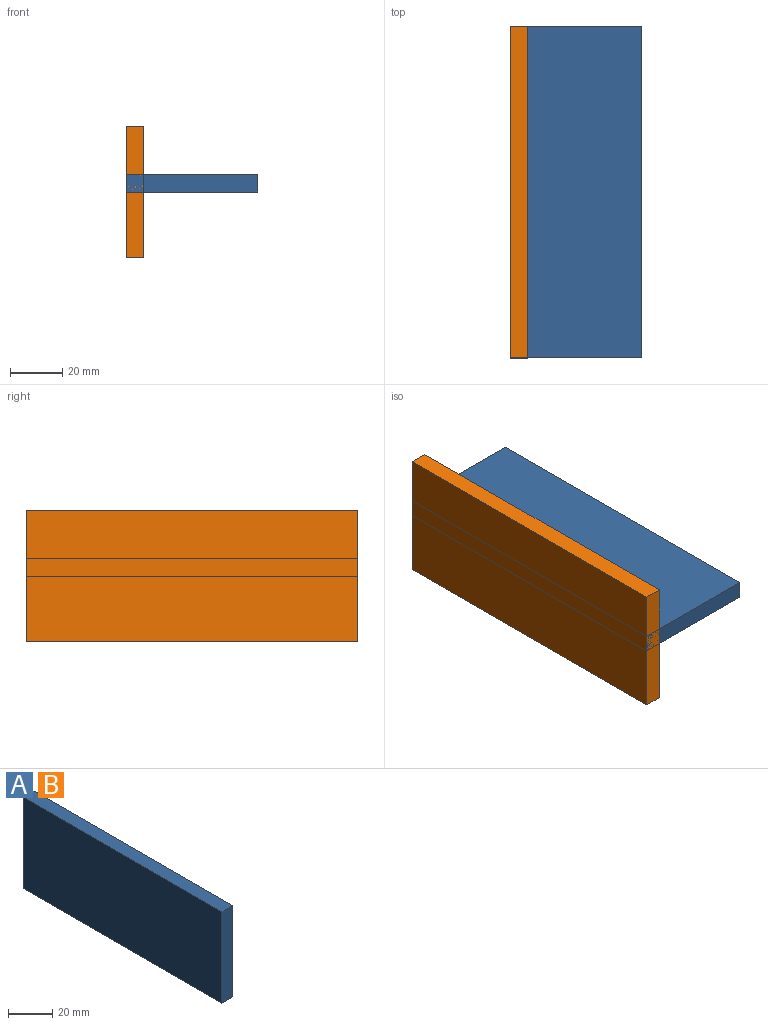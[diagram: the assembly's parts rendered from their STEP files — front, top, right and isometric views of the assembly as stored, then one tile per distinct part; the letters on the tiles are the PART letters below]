
ASSEMBLY  parts=2 mates=2
PART A: 6 faces, bbox 6.9x127x50.5 mm
  f0: plane 127x50.5mm, normal (-1,0,0), area 6412.9mm2, adj f1,f3,f4,f5
  f1: plane 127x6.85mm, normal (0,0,-1), area 870.1mm2, adj f0,f2,f4,f5
  f2: plane 127x50.5mm, normal (1,0,0), area 6412.9mm2, adj f1,f3,f4,f5
  f3: plane 127x6.85mm, normal (0,0,1), area 870.1mm2, adj f0,f2,f4,f5
  f4: plane 50.5x6.85mm, normal (0,-1,0), area 345.9mm2, adj f0,f1,f2,f3
  f5: plane 50.5x6.85mm, normal (0,1,0), area 345.9mm2, adj f0,f1,f2,f3
PART B: same geometry as A
PLACE A rot(axis=(0,1,0),90deg) t=(30.49,-3.83,17.42)mm
PLACE B t=(26.67,-3.83,2.85)mm
MATE planar A.f1 <-> B.f0  axis (-1,0,0) through (19.82,-67.33,20.85)mm
MATE planar B.f5 <-> A.f5  axis (0,1,0) through (26.67,-3.83,17.42)mm
